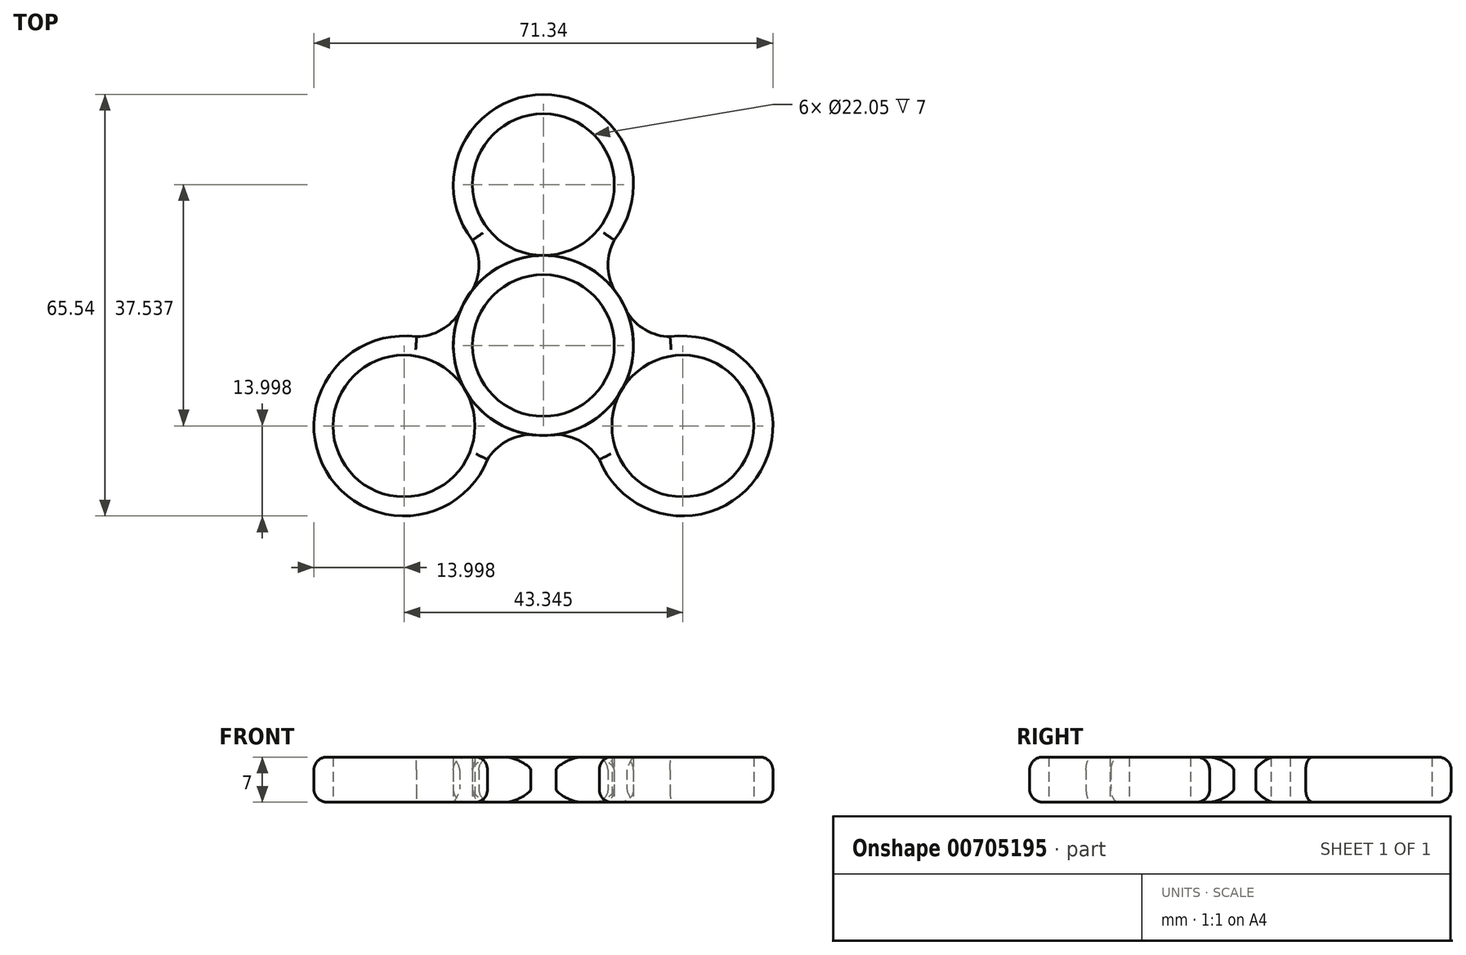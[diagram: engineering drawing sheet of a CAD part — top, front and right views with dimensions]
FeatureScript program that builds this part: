
annotation { "Feature Type Name" : "Feature", "Feature Type Description" : "" }
export const myFeature = defineFeature(function(context is Context, id is Id, definition is map)
    precondition{}
    {
        {
            var Q0;
            Q0=qCreatedBy(makeId("Top.planeOp"),FACE);
            var sketch = newSketch(context, id + "F0", { "sketchPlane" : qUnion([Q0])});
            skCircle(sketch, "E0", {"center": v(0, 0) * mm, "radius": 11.03 * mm});
            skCircle(sketch, "E1", {"center": v(0, 0) * mm, "radius": 14 * mm});
            skCircle(sketch, "E2", {"center": v(0, 25.02) * mm, "radius": 11.03 * mm});
            skCircle(sketch, "E3", {"center": v(0, 25.02) * mm, "radius": 14 * mm});
            skArc(sketch, "E4", {"start": v(-11.03, 8.63) * mm, "mid": v(-10.03, 12.51) * mm, "end": v(-11.03, 16.4) * mm});
            skArc(sketch, "E5.MirrorCS", {"start": v(11.03, 8.63) * mm, "mid": v(10.03, 12.51) * mm, "end": v(11.03, 16.4) * mm});
            skSolve(sketch);
        }
        {
            var Q0;
            Q0 = qSketchRegion(id + "F0", true);
            var Q1;
            {var subQ0=sQuery(id+"F0.wireOp",EDGE,"E1");var subQ1=makeQuery(id+"F0.imprint","INTERSECT",VERTEX,{"derivedFrom":[subQ0,sQuery(id+"F0.wireOp",EDGE,"E2")]});Q1=makeQuery(id+"F0.imprint","IMPRINT",FACE,{"disambiguationData":[TD([[makeQuery(id+"F0.imprint","IMPRINT",EDGE,{"disambiguationData":[TD([[subQ1,1.0]])],"derivedFrom":subQ0}),1.0]])]});}
            extrude(context, id + "F1", {"entities" : qUnion([Q0, Q1]), "depth" : 7 * mm, "offsetDistance" : 25 * mm});
        }
        {
            var Q0;
            Q0=makeQuery(id+"F1.opExtrude","SWEPT_BODY",BODY,{"disambiguationData":[OSD([sQuery(id+"F0.wireOp",EDGE,"E0"),sQuery(id+"F0.wireOp",EDGE,"E1"),sQuery(id+"F0.wireOp",EDGE,"E2"),sQuery(id+"F0.wireOp",EDGE,"E3"),sQuery(id+"F0.wireOp",EDGE,"E4"),sQuery(id+"F0.wireOp",EDGE,"E5.MirrorCS")])]});
            var Q1;
            Q1=makeQuery(id+"F1.opExtrude","SWEPT_FACE",FACE,{"disambiguationData":[OSD([sQuery(id+"F0.wireOp",EDGE,"E1")])]});
            circularPattern(context, id + "F2", {"entities" : qUnion([Q0]), "axis" : qUnion([Q1]), "angle" : 360 * degree, "instanceCount" : 3, "equalSpace" : true});
        }
        {
            var Q0;
            Q0=makeQuery(id+"F1.opExtrude","CAP_EDGE",EDGE,{"disambiguationData":[OSD([sQuery(id+"F0.wireOp",EDGE,"E3")])],"isStart":false});
            var Q1;
            Q1=makeQuery(id+"F2.opPattern","COPY",EDGE,{"derivedFrom":makeQuery(id+"F1.opExtrude","CAP_EDGE",EDGE,{"disambiguationData":[OSD([sQuery(id+"F0.wireOp",EDGE,"E3")])],"isStart":false}),"instanceName":"2"});
            var Q2;
            Q2=makeQuery(id+"F2.opPattern","COPY",EDGE,{"derivedFrom":makeQuery(id+"F1.opExtrude","CAP_EDGE",EDGE,{"disambiguationData":[OSD([sQuery(id+"F0.wireOp",EDGE,"E5.MirrorCS")])],"isStart":false}),"instanceName":"2"});
            var Q3;
            Q3=makeQuery(id+"F1.opExtrude","CAP_EDGE",EDGE,{"disambiguationData":[OSD([sQuery(id+"F0.wireOp",EDGE,"E4")])],"isStart":false});
            var Q4;
            Q4=makeQuery(id+"F2.opPattern","COPY",EDGE,{"derivedFrom":makeQuery(id+"F1.opExtrude","CAP_EDGE",EDGE,{"disambiguationData":[OSD([sQuery(id+"F0.wireOp",EDGE,"E4")])],"isStart":false}),"instanceName":"2"});
            var Q5;
            Q5=makeQuery(id+"F2.opPattern","COPY",EDGE,{"derivedFrom":makeQuery(id+"F1.opExtrude","CAP_EDGE",EDGE,{"disambiguationData":[OSD([sQuery(id+"F0.wireOp",EDGE,"E5.MirrorCS")])],"isStart":false}),"instanceName":"1"});
            var Q6;
            Q6=makeQuery(id+"F2.opPattern","COPY",EDGE,{"derivedFrom":makeQuery(id+"F1.opExtrude","CAP_EDGE",EDGE,{"disambiguationData":[OSD([sQuery(id+"F0.wireOp",EDGE,"E3")])],"isStart":false}),"instanceName":"1"});
            var Q7;
            Q7=makeQuery(id+"F2.opPattern","COPY",EDGE,{"derivedFrom":makeQuery(id+"F1.opExtrude","CAP_EDGE",EDGE,{"disambiguationData":[OSD([sQuery(id+"F0.wireOp",EDGE,"E4")])],"isStart":false}),"instanceName":"1"});
            var Q8;
            Q8=makeQuery(id+"F1.opExtrude","CAP_EDGE",EDGE,{"disambiguationData":[OSD([sQuery(id+"F0.wireOp",EDGE,"E5.MirrorCS")])],"isStart":false});
            var Q9;
            Q9=makeQuery(id+"F2.opPattern","COPY",EDGE,{"derivedFrom":makeQuery(id+"F1.opExtrude","CAP_EDGE",EDGE,{"disambiguationData":[OSD([sQuery(id+"F0.wireOp",EDGE,"E4")])],"isStart":true}),"instanceName":"1"});
            var Q10;
            Q10=makeQuery(id+"F2.opPattern","COPY",EDGE,{"derivedFrom":makeQuery(id+"F1.opExtrude","CAP_EDGE",EDGE,{"disambiguationData":[OSD([sQuery(id+"F0.wireOp",EDGE,"E3")])],"isStart":true}),"instanceName":"1"});
            var Q11;
            Q11=makeQuery(id+"F2.opPattern","COPY",EDGE,{"derivedFrom":makeQuery(id+"F1.opExtrude","CAP_EDGE",EDGE,{"disambiguationData":[OSD([sQuery(id+"F0.wireOp",EDGE,"E5.MirrorCS")])],"isStart":true}),"instanceName":"1"});
            var Q12;
            Q12=makeQuery(id+"F2.opPattern","COPY",EDGE,{"derivedFrom":makeQuery(id+"F1.opExtrude","CAP_EDGE",EDGE,{"disambiguationData":[OSD([sQuery(id+"F0.wireOp",EDGE,"E4")])],"isStart":true}),"instanceName":"2"});
            var Q13;
            Q13=makeQuery(id+"F2.opPattern","COPY",EDGE,{"derivedFrom":makeQuery(id+"F1.opExtrude","CAP_EDGE",EDGE,{"disambiguationData":[OSD([sQuery(id+"F0.wireOp",EDGE,"E3")])],"isStart":true}),"instanceName":"2"});
            var Q14;
            Q14=makeQuery(id+"F2.opPattern","COPY",EDGE,{"derivedFrom":makeQuery(id+"F1.opExtrude","CAP_EDGE",EDGE,{"disambiguationData":[OSD([sQuery(id+"F0.wireOp",EDGE,"E5.MirrorCS")])],"isStart":true}),"instanceName":"2"});
            var Q15;
            Q15=makeQuery(id+"F1.opExtrude","CAP_EDGE",EDGE,{"disambiguationData":[OSD([sQuery(id+"F0.wireOp",EDGE,"E4")])],"isStart":true});
            var Q16;
            Q16=makeQuery(id+"F1.opExtrude","CAP_EDGE",EDGE,{"disambiguationData":[OSD([sQuery(id+"F0.wireOp",EDGE,"E3")])],"isStart":true});
            var Q17;
            Q17=makeQuery(id+"F1.opExtrude","CAP_EDGE",EDGE,{"disambiguationData":[OSD([sQuery(id+"F0.wireOp",EDGE,"E5.MirrorCS")])],"isStart":true});
            fillet(context, id + "F3", {"entities" : qUnion([Q0, Q1, Q2, Q3, Q4, Q5, Q6, Q7, Q8, Q9, Q10, Q11, Q12, Q13, Q14, Q15, Q16, Q17]), "radius" : 2 * mm, "tangentPropagation" : true, "allowEdgeOverflow" : false});
        }
    });
